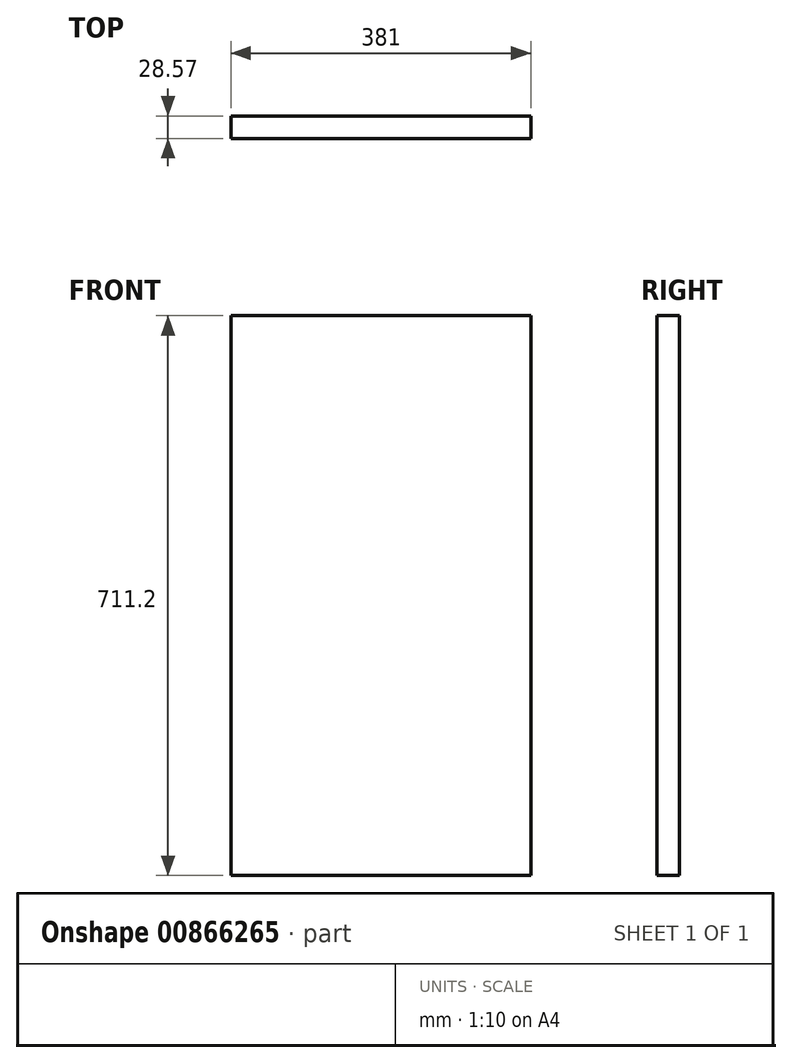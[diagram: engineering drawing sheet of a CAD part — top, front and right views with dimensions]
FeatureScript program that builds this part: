
annotation { "Feature Type Name" : "Feature", "Feature Type Description" : "" }
export const myFeature = defineFeature(function(context is Context, id is Id, definition is map)
    precondition{}
    {
        {
            var Q0;
            Q0=qCreatedBy(makeId("Front.planeOp"),FACE);
            var sketch = newSketch(context, id + "F0", { "sketchPlane" : qUnion([Q0])});
            skLineSegment(sketch, "E0.bottom", {"start": v(190.5, 355.6) * mm, "end": v(-190.5, 355.6) * mm});
            skLineSegment(sketch, "E0.top", {"start": v(190.5, -355.6) * mm, "end": v(-190.5, -355.6) * mm});
            skLineSegment(sketch, "E0.left", {"start": v(190.5, 355.6) * mm, "end": v(190.5, -355.6) * mm});
            skLineSegment(sketch, "E0.right", {"start": v(-190.5, 355.6) * mm, "end": v(-190.5, -355.6) * mm});
            skPoint(sketch, "E0.middle", {"position": v(0, 0) * mm});
            skSolve(sketch);
        }
        {
            var Q0;
            Q0=makeQuery(id+"F0.imprint","IMPRINT",FACE,{"disambiguationData":[TD([[makeQuery(id+"F0.imprint","IMPRINT",EDGE,{"derivedFrom":sQuery(id+"F0.wireOp",EDGE,"E0.bottom")}),1.0]])]});
            extrude(context, id + "F1", {"entities" : qUnion([Q0]), "depth" : 28.57 * mm, "offsetDistance" : 25.4 * mm});
        }
    });
